# Revit family: Kessel AG 48904 en
name_source: partatom
category: Sanitärinstallationen
revit_build: Autodesk Revit 2014 (Build: 20130308_1515(x64)
units: mm (PartAtom-declared; Revit-internal decimal feet)

## types (1)
- Kessel AG 48904 en
    <1.010.00.2> Number of the part of the guideline = 38
    <1.010.00.3> Issue date (month) of the guideline = 201805
    <1.010.00.4> Manufacturer name = Kessel AG
    <1.010.00.5> Revision date of the file = 20181105
    <1.800.00.3> BS number = 1020010000000000000000000000000000000000000000000200000000
    <1.800.00.4> Comment field = Dünnbett-Aufsatzstück Variofix Designrost Kessel, V2A, Lock & Lift, L15
    <1.810.00.3> Manufacturer’s reference number = 48904
    <1.810.00.4> DATANORM number = 48904
    <1.810.00.6> GTIN number = 4026092028841
    <1.960/3L.00.8> Link (URL) = http://www.kessel.de
    <38.100.00.4> Drain type for floor, roof and sanitary objects = Zubehör
    <38.110.00.4> Floor, roof and sanitary works sequences = Zubehör
    <38.700.00.15> Connection to GLT, GA = no
    <38.700.00.16> Fire resistance class can be retrofitted = no
    <38.700.00.4> product name = Dünnbett-Aufsatzstück Variofix Designrost Kessel, V2A, Lock & Lift, L15
    <38.700.00.6> Complete article (one-piece) from combination (multi-part design) Drain body and attachment piece = no
    <38.700.00.7> Potential compensation (ground connection) available = no
    <38.700.00.8> Electrical connection = no
    Hersteller = Kessel AG
    Modell = 48904
    URL = www.kessel.de
